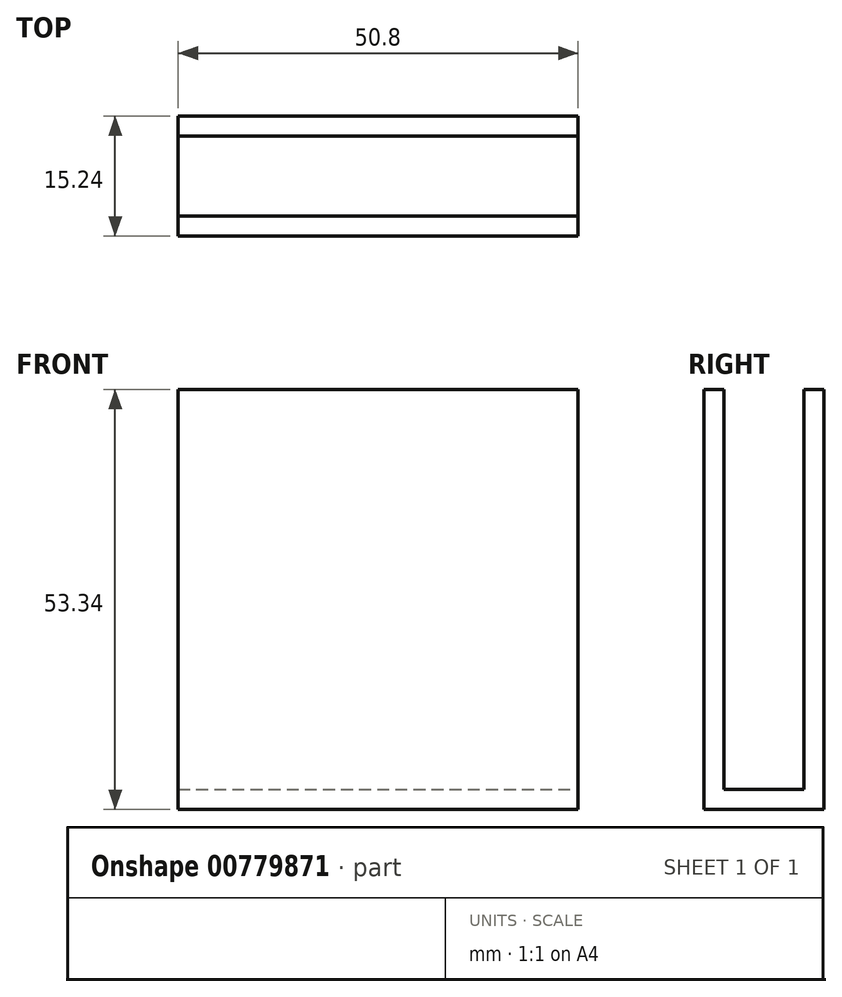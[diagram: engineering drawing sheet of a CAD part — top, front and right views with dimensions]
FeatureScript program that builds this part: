
annotation { "Feature Type Name" : "Feature", "Feature Type Description" : "" }
export const myFeature = defineFeature(function(context is Context, id is Id, definition is map)
    precondition{}
    {
        {
            var Q0;
            Q0=qCreatedBy(makeId("Top.planeOp"),FACE);
            var sketch = newSketch(context, id + "F0", { "sketchPlane" : qUnion([Q0])});
            skLineSegment(sketch, "E0.bottom", {"start": v(-17.7, 0.51) * mm, "end": v(33.1, 0.51) * mm});
            skLineSegment(sketch, "E0.top", {"start": v(-17.7, -14.73) * mm, "end": v(33.1, -14.73) * mm});
            skLineSegment(sketch, "E0.left", {"start": v(-17.7, 0.51) * mm, "end": v(-17.7, -14.73) * mm});
            skLineSegment(sketch, "E0.right", {"start": v(33.1, 0.51) * mm, "end": v(33.1, -14.73) * mm});
            skSolve(sketch);
        }
        {
            var Q0;
            Q0 = qSketchRegion(id + "F0", true);
            extrude(context, id + "F1", {"entities" : qUnion([Q0]), "depth" : 2.54 * mm, "offsetDistance" : 25.4 * mm});
        }
        {
            var Q0;
            Q0=makeQuery(id+"F1.opExtrude","CAP_FACE",FACE,{"disambiguationData":[OSD([sQuery(id+"F0.wireOp",EDGE,"E0.bottom"),sQuery(id+"F0.wireOp",EDGE,"E0.top"),sQuery(id+"F0.wireOp",EDGE,"E0.left"),sQuery(id+"F0.wireOp",EDGE,"E0.right")])],"isStart":false});
            var sketch = newSketch(context, id + "F2", { "sketchPlane" : qUnion([Q0])});
            skLineSegment(sketch, "E1.bottom", {"start": v(-17.7, 0.51) * mm, "end": v(33.1, 0.51) * mm});
            skLineSegment(sketch, "E1.top", {"start": v(-17.7, -2.03) * mm, "end": v(33.1, -2.03) * mm});
            skLineSegment(sketch, "E1.left", {"start": v(-17.7, 0.51) * mm, "end": v(-17.7, -2.03) * mm});
            skLineSegment(sketch, "E1.right", {"start": v(33.1, 0.51) * mm, "end": v(33.1, -2.03) * mm});
            skLineSegment(sketch, "E2.bottom", {"start": v(-17.7, -14.73) * mm, "end": v(33.1, -14.73) * mm});
            skLineSegment(sketch, "E2.top", {"start": v(-17.7, -12.19) * mm, "end": v(33.1, -12.19) * mm});
            skLineSegment(sketch, "E2.left", {"start": v(-17.7, -14.73) * mm, "end": v(-17.7, -12.19) * mm});
            skLineSegment(sketch, "E2.right", {"start": v(33.1, -14.73) * mm, "end": v(33.1, -12.19) * mm});
            skSolve(sketch);
        }
        {
            var Q0;
            Q0=makeQuery(id+"F2.imprint","IMPRINT",FACE,{"disambiguationData":[TD([[makeQuery(id+"F2.imprint","IMPRINT",EDGE,{"derivedFrom":sQuery(id+"F2.wireOp",EDGE,"E2.bottom")}),1.0]])]});
            var Q1;
            Q1=makeQuery(id+"F2.imprint","IMPRINT",FACE,{"disambiguationData":[TD([[makeQuery(id+"F2.imprint","IMPRINT",EDGE,{"derivedFrom":sQuery(id+"F2.wireOp",EDGE,"E1.bottom")}),-1.0]])]});
            extrude(context, id + "F3", {"entities" : qUnion([Q0, Q1]), "operationType" : NewBodyOperationType.ADD, "depth" : 50.8 * mm, "offsetDistance" : 25.4 * mm});
        }
    });
